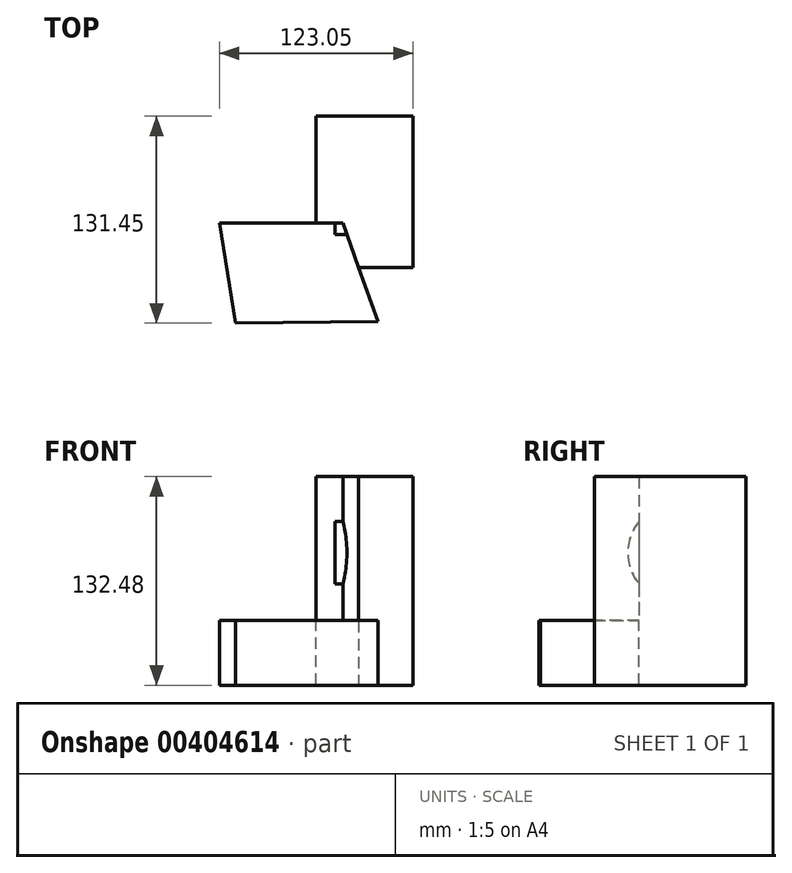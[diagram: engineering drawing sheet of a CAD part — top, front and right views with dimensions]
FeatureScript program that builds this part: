
annotation { "Feature Type Name" : "Feature", "Feature Type Description" : "" }
export const myFeature = defineFeature(function(context is Context, id is Id, definition is map)
    precondition{}
    {
        {
            var Q0;
            Q0=qCreatedBy(makeId("Top.planeOp"),FACE);
            var sketch = newSketch(context, id + "F0", { "sketchPlane" : qUnion([Q0])});
            skLineSegment(sketch, "E0", {"start": v(-49.53, -63.57) * mm, "end": v(-59.84, 0) * mm});
            skLineSegment(sketch, "E1", {"start": v(-59.84, 0) * mm, "end": v(18.54, 0) * mm});
            skLineSegment(sketch, "E2", {"start": v(18.54, 0) * mm, "end": v(40.94, -62.6) * mm});
            skLineSegment(sketch, "E3", {"start": v(40.94, -62.6) * mm, "end": v(-49.53, -63.57) * mm});
            skSolve(sketch);
        }
        {
            var Q0;
            Q0=makeQuery(id+"F0.imprint","IMPRINT",FACE,{"disambiguationData":[TD([[makeQuery(id+"F0.imprint","IMPRINT",EDGE,{"derivedFrom":sQuery(id+"F0.wireOp",EDGE,"E0")}),-1.0]])]});
            extrude(context, id + "F1", {"entities" : qUnion([Q0]), "depth" : 41.06 * mm});
        }
        {
            var Q0;
            Q0=qCreatedBy(makeId("Top.planeOp"),FACE);
            var sketch = newSketch(context, id + "F2", { "sketchPlane" : qUnion([Q0])});
            skLineSegment(sketch, "E4.bottom", {"start": v(63.2, -28.28) * mm, "end": v(1.4, -28.28) * mm});
            skLineSegment(sketch, "E4.top", {"start": v(63.2, 67.88) * mm, "end": v(1.4, 67.88) * mm});
            skLineSegment(sketch, "E4.left", {"start": v(63.2, -28.28) * mm, "end": v(63.2, 67.88) * mm});
            skLineSegment(sketch, "E4.right", {"start": v(1.4, -28.28) * mm, "end": v(1.4, 67.88) * mm});
            skPoint(sketch, "E4.middle", {"position": v(32.3, 19.8) * mm});
            skSolve(sketch);
        }
        {
            var Q0;
            Q0 = qSketchRegion(id + "F2", true);
            extrude(context, id + "F3", {"entities" : qUnion([Q0]), "operationType" : NewBodyOperationType.ADD, "depth" : 25.4 * mm});
        }
        {
            var Q0;
            Q0=makeQuery(id+"F3.opExtrude","CAP_FACE",FACE,{"disambiguationData":[OSD([sQuery(id+"F2.wireOp",EDGE,"E4.bottom"),sQuery(id+"F2.wireOp",EDGE,"E4.top"),sQuery(id+"F2.wireOp",EDGE,"E4.left"),sQuery(id+"F2.wireOp",EDGE,"E4.right")])],"isStart":false});
            extrude(context, id + "F4", {"entities" : qUnion([Q0]), "operationType" : NewBodyOperationType.ADD, "depth" : 76.47 * mm});
        }
        {
            var Q0;
            Q0=makeQuery(id+"F4.opExtrude","CAP_FACE",FACE,{"disambiguationData":[OSD([sQuery(id+"F2.wireOp",EDGE,"E4.bottom"),sQuery(id+"F2.wireOp",EDGE,"E4.top"),sQuery(id+"F2.wireOp",EDGE,"E4.left"),sQuery(id+"F2.wireOp",EDGE,"E4.right")])],"isStart":false});
            var sketch = newSketch(context, id + "F5", { "sketchPlane" : qUnion([Q0])});
            skSolve(sketch);
        }
        {
            var Q0;
            {var subQ3=sQuery(id+"F2.wireOp",EDGE,"E4.top");Q0=makeQuery(id+"F5.imprint","IMPRINT",FACE,{"disambiguationData":[TD([[makeQuery(id+"F5.imprint","IMPRINT",EDGE,{"derivedFrom":makeQuery(id+"F4.opExtrude","CAP_EDGE",EDGE,{"disambiguationData":[OSD([subQ3])],"isStart":false})}),1.0]])]});}
            extrude(context, id + "F6", {"entities" : qUnion([Q0]), "operationType" : NewBodyOperationType.ADD, "depth" : 30.6 * mm});
        }
        {
            var Q0;
            {var subQ0=sQuery(id+"F2.wireOp",EDGE,"E4.left");Q0=makeQuery(id+"F6.boolean.opBoolean","MERGE",FACE,{"derivedFrom":[makeQuery(id+"F4.boolean.opBoolean","MERGE",FACE,{"derivedFrom":[makeQuery(id+"F3.opExtrude","SWEPT_FACE",FACE,{"disambiguationData":[OSD([subQ0])]}),makeQuery(id+"F4.opExtrude","SWEPT_FACE",FACE,{"disambiguationData":[OSD([subQ0])]})]}),makeQuery(id+"F6.opExtrude","SWEPT_FACE",FACE,{"disambiguationData":[OSD([subQ0])]})]});}
            var sketch = newSketch(context, id + "F7", { "sketchPlane" : qUnion([Q0])});
            skCircle(sketch, "E5", {"center": v(23.3, 84.2) * mm, "radius": 30.61 * mm});
            skSolve(sketch);
        }
        {
            var Q0;
            Q0=makeQuery(id+"F7.imprint","IMPRINT",FACE,{"disambiguationData":[TD([[makeQuery(id+"F7.imprint","IMPRINT",EDGE,{"derivedFrom":sQuery(id+"F7.wireOp",EDGE,"E5")}),1.0]])]});
            var sketch = newSketch(context, id + "F8", { "sketchPlane" : qUnion([Q0])});
            skSolve(sketch);
        }
        {
            var Q0;
            Q0=makeQuery(id+"F8.imprint","IMPRINT",FACE,{"disambiguationData":[TD([[makeQuery(id+"F8.imprint","IMPRINT",EDGE,{"derivedFrom":makeQuery(id+"F7.imprint","IMPRINT",EDGE,{"derivedFrom":sQuery(id+"F7.wireOp",EDGE,"E5")})}),1.0]])]});
            extrude(context, id + "F9", {"entities" : qUnion([Q0]), "operationType" : NewBodyOperationType.ADD, "oppositeDirection" : true, "depth" : 49.64 * mm});
        }
    });
